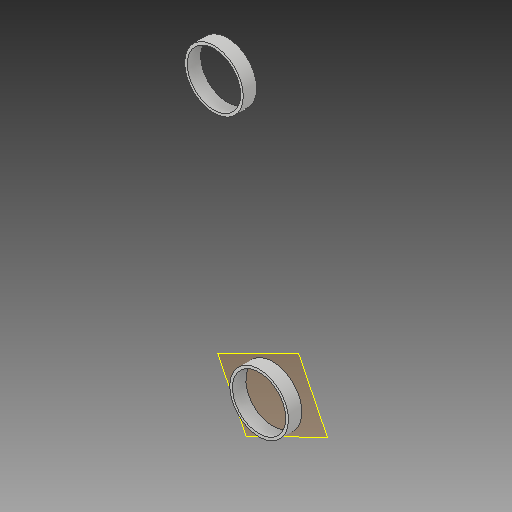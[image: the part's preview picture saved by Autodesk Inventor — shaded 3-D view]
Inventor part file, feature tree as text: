
AUTODESK INVENTOR PART (.ipt)
format: ipt  version: 2019.3 (Build 233278000, 278)  size: 107,520 bytes
history: native  units: mm
features: other x4, extrude x2, sketch x2, reference x2, plane x1
ambient origin geometry x8: Origin, YZ Plane, XZ Plane, XY Plane, X Axis, Y Axis, Z Axis, Center Point
bodies: Solid1 (feature_tree)
feature tree (11):
  extrude  "Extrusion1"  Depth=4.0mm TaperAngle=0.0deg
  plane  "Work Plane1"
  extrude  "Extrusion2"  [1 undecoded]
  sketch  "Sketch1"  dims[d0=4.0mm d1=0.0mm d3=4.0mm d4=0.0mm]
  reference  "Reference1"
  sketch  "Sketch2"
  reference  "Reference2"
  parser-record x1  (decoder bookkeeping rows leaked as tree rows — omitted from the tree; the rows remain in map.json)
  other  "mount assem.iam"
  other  "94695A250_TYPE 316 STAINLESS STEEL COUNTERSUNK WASHER:2"
  other  "94695A250_TYPE 316 STAINLESS STEEL COUNTERSUNK WASHER:1"
note: 1 required parameter value undecoded (feature->parameter linkage not recoverable at this tier; creation-order binding heuristic only, values carry confidence <= 0.55)
note: 1 file-system path scrubbed to <path> (originals preserved in map.json)
